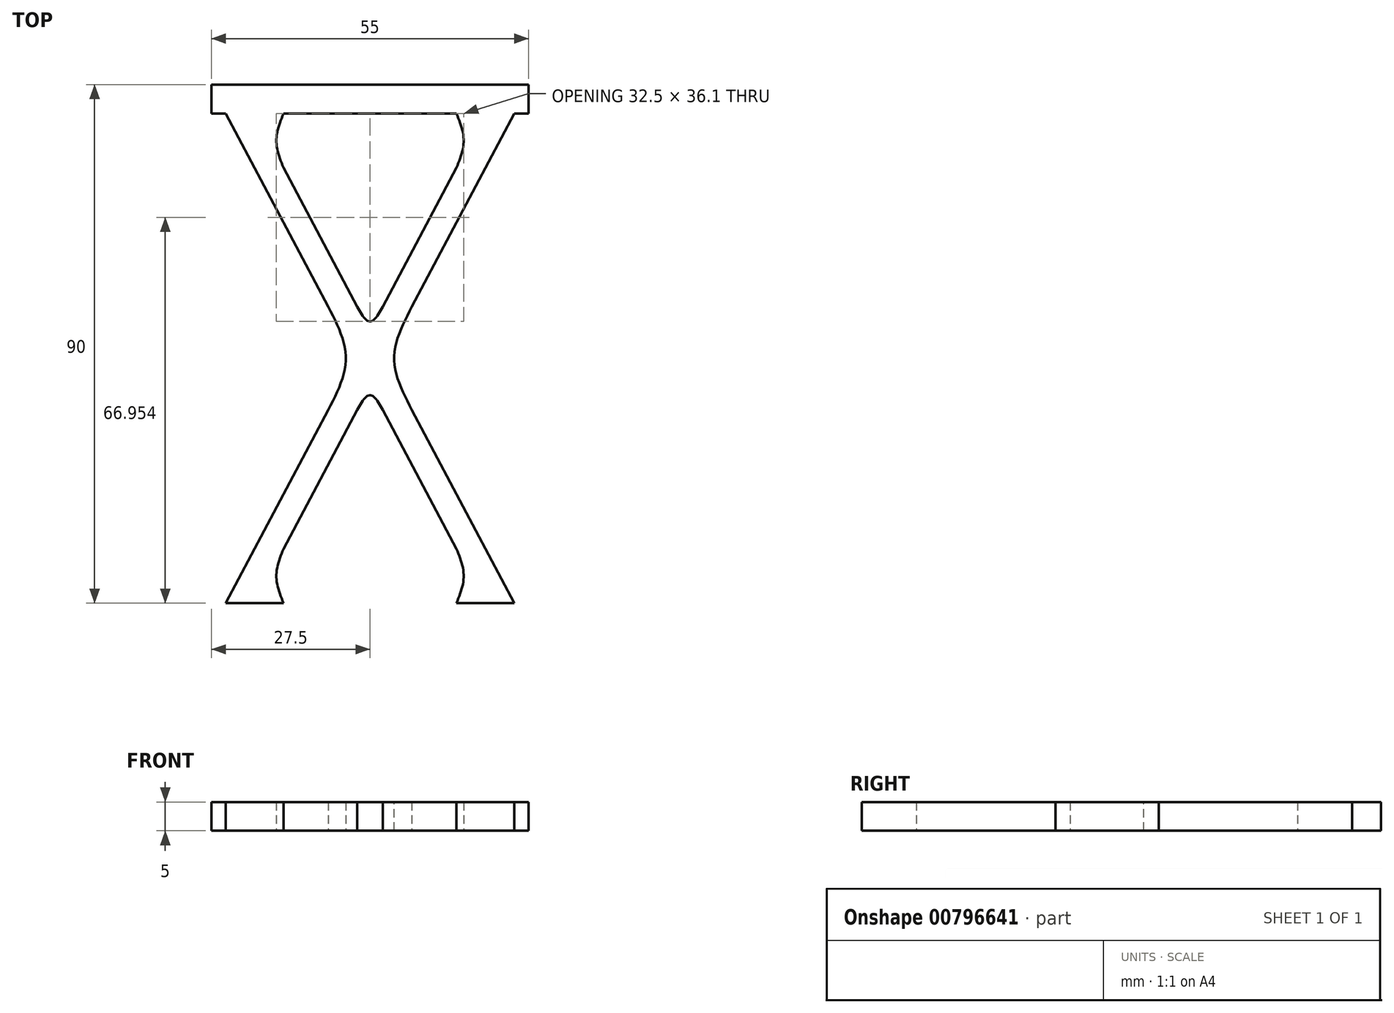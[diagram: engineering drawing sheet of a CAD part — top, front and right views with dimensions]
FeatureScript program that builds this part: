
annotation { "Feature Type Name" : "Feature", "Feature Type Description" : "" }
export const myFeature = defineFeature(function(context is Context, id is Id, definition is map)
    precondition{}
    {
        {
            var Q0;
            Q0=qCreatedBy(makeId("Top.planeOp"),FACE);
            var sketch = newSketch(context, id + "F0", { "sketchPlane" : qUnion([Q0])});
            skLineSegment(sketch, "E0.bottom", {"start": v(-698.92, -298.79) * mm, "end": v(-643.92, -298.79) * mm});
            skLineSegment(sketch, "E1", {"start": v(-696.42, -383.79) * mm, "end": v(-691.42, -383.79) * mm});
            skLineSegment(sketch, "E2", {"start": v(-691.42, -383.79) * mm, "end": v(-686.42, -383.79) * mm});
            skLineSegment(sketch, "E3", {"start": v(-646.42, -383.79) * mm, "end": v(-651.42, -383.79) * mm});
            skLineSegment(sketch, "E4", {"start": v(-651.42, -383.79) * mm, "end": v(-656.42, -383.79) * mm});
            skLineSegment(sketch, "E5", {"start": v(-698.92, -298.79) * mm, "end": v(-696.42, -298.79) * mm});
            skLineSegment(sketch, "E6", {"start": v(-696.42, -298.79) * mm, "end": v(-691.42, -298.79) * mm});
            skLineSegment(sketch, "E7", {"start": v(-691.42, -298.79) * mm, "end": v(-686.42, -298.79) * mm});
            skLineSegment(sketch, "E8", {"start": v(-643.92, -298.79) * mm, "end": v(-646.42, -298.79) * mm});
            skLineSegment(sketch, "E9", {"start": v(-646.42, -298.79) * mm, "end": v(-651.42, -298.79) * mm});
            skLineSegment(sketch, "E10", {"start": v(-651.42, -298.79) * mm, "end": v(-656.42, -298.79) * mm});
            skLineSegment(sketch, "E11", {"start": v(-646.42, -383.79) * mm, "end": v(-691.42, -298.79) * mm});
            skLineSegment(sketch, "E12", {"start": v(-646.42, -298.79) * mm, "end": v(-691.42, -383.79) * mm});
            skLineSegment(sketch, "E13", {"start": v(-696.42, -383.79) * mm, "end": v(-651.42, -298.79) * mm});
            skLineSegment(sketch, "E14", {"start": v(-696.42, -298.79) * mm, "end": v(-651.42, -383.79) * mm});
            skLineSegment(sketch, "E15", {"start": v(-686.42, -374.34) * mm, "end": v(-688.92, -379.06) * mm});
            skFitSpline(sketch, "E16", {"points": [v(-686.42, -383.79) * mm, v(-687.67, -379.06) * mm, v(-686.42, -374.34) * mm], "startDerivative": vector(-3.75, 9.44) * mm, "endDerivative": vector(3.75, 9.44) * mm});
            skFitSpline(sketch, "E17", {"points": [v(-656.42, -383.79) * mm, v(-655.17, -379.06) * mm, v(-656.42, -374.34) * mm], "startDerivative": vector(3.75, 9.44) * mm, "endDerivative": vector(-3.75, 9.44) * mm});
            skFitSpline(sketch, "E18", {"points": [v(-686.42, -298.79) * mm, v(-687.67, -303.5) * mm, v(-686.42, -308.23) * mm], "startDerivative": vector(-3.75, -9.44) * mm, "endDerivative": vector(3.75, -9.44) * mm});
            skFitSpline(sketch, "E19", {"points": [v(-656.42, -298.79) * mm, v(-655.17, -303.5) * mm, v(-656.42, -308.23) * mm], "startDerivative": vector(3.75, -9.44) * mm, "endDerivative": vector(-3.75, -9.44) * mm});
            skLineSegment(sketch, "E20", {"start": v(-673.92, -341.29) * mm, "end": v(-678.66, -332.34) * mm});
            skLineSegment(sketch, "E21", {"start": v(-678.66, -350.23) * mm, "end": v(-673.92, -341.29) * mm});
            skFitSpline(sketch, "E22", {"points": [v(-678.66, -332.34) * mm, v(-675.6, -341.29) * mm, v(-678.66, -350.23) * mm], "startDerivative": vector(9.19, -17.9) * mm, "endDerivative": vector(-9.19, -17.9) * mm});
            skFitSpline(sketch, "E23", {"points": [v(-664.18, -332.34) * mm, v(-667.24, -341.29) * mm, v(-664.18, -350.23) * mm], "startDerivative": vector(-9.18, -17.9) * mm, "endDerivative": vector(9.18, -17.9) * mm});
            skFitSpline(sketch, "E24", {"points": [v(-673.66, -332.34) * mm, v(-671.42, -334.89) * mm, v(-669.18, -332.34) * mm], "startDerivative": vector(4.47, -7.65) * mm, "endDerivative": vector(4.47, 7.65) * mm});
            skFitSpline(sketch, "E25", {"points": [v(-673.66, -350.23) * mm, v(-671.42, -347.68) * mm, v(-669.18, -350.23) * mm], "startDerivative": vector(4.47, 7.65) * mm, "endDerivative": vector(4.47, -7.65) * mm});
            skLineSegment(sketch, "E26.top", {"start": v(-698.92, -293.79) * mm, "end": v(-643.92, -293.79) * mm});
            skLineSegment(sketch, "E26.left", {"start": v(-698.92, -298.79) * mm, "end": v(-698.92, -293.79) * mm});
            skLineSegment(sketch, "E26.right", {"start": v(-643.92, -298.79) * mm, "end": v(-643.92, -293.79) * mm});
            skSolve(sketch);
        }
        {
            var Q0;
            Q0 = qSketchRegion(id + "F0", true);
            var Q1;
            {var subQ0=sQuery(id+"F0.wireOp",EDGE,"E12");var subQ1=sQuery(id+"F0.wireOp",EDGE,"E11");var subQ2=makeQuery(id+"F0.imprint","INTERSECT",VERTEX,{"derivedFrom":[subQ1,subQ0]});Q1=makeQuery(id+"F0.imprint","IMPRINT",FACE,{"disambiguationData":[TD([[makeQuery(id+"F0.imprint","IMPRINT",EDGE,{"disambiguationData":[TD([[subQ2,-1.0]])],"derivedFrom":subQ1}),1.0]])]});}
            var Q2;
            {var subQ3=sQuery(id+"F0.wireOp",EDGE,"E18");Q2=makeQuery(id+"F0.imprint","IMPRINT",FACE,{"disambiguationData":[TD([[makeQuery(id+"F0.imprint","IMPRINT",EDGE,{"derivedFrom":subQ3}),-1.0]])]});}
            var Q3;
            {var subQ3=sQuery(id+"F0.wireOp",EDGE,"E19");Q3=makeQuery(id+"F0.imprint","IMPRINT",FACE,{"disambiguationData":[TD([[makeQuery(id+"F0.imprint","IMPRINT",EDGE,{"derivedFrom":subQ3}),1.0]])]});}
            var Q4;
            {var subQ0=sQuery(id+"F0.wireOp",EDGE,"E24");Q4=makeQuery(id+"F0.imprint","IMPRINT",FACE,{"disambiguationData":[TD([[makeQuery(id+"F0.imprint","IMPRINT",EDGE,{"derivedFrom":subQ0}),-1.0]])]});}
            extrude(context, id + "F1", {"entities" : qUnion([Q0, Q1, Q2, Q3, Q4]), "depth" : 5 * mm, "offsetDistance" : 25.4 * mm});
        }
    });
